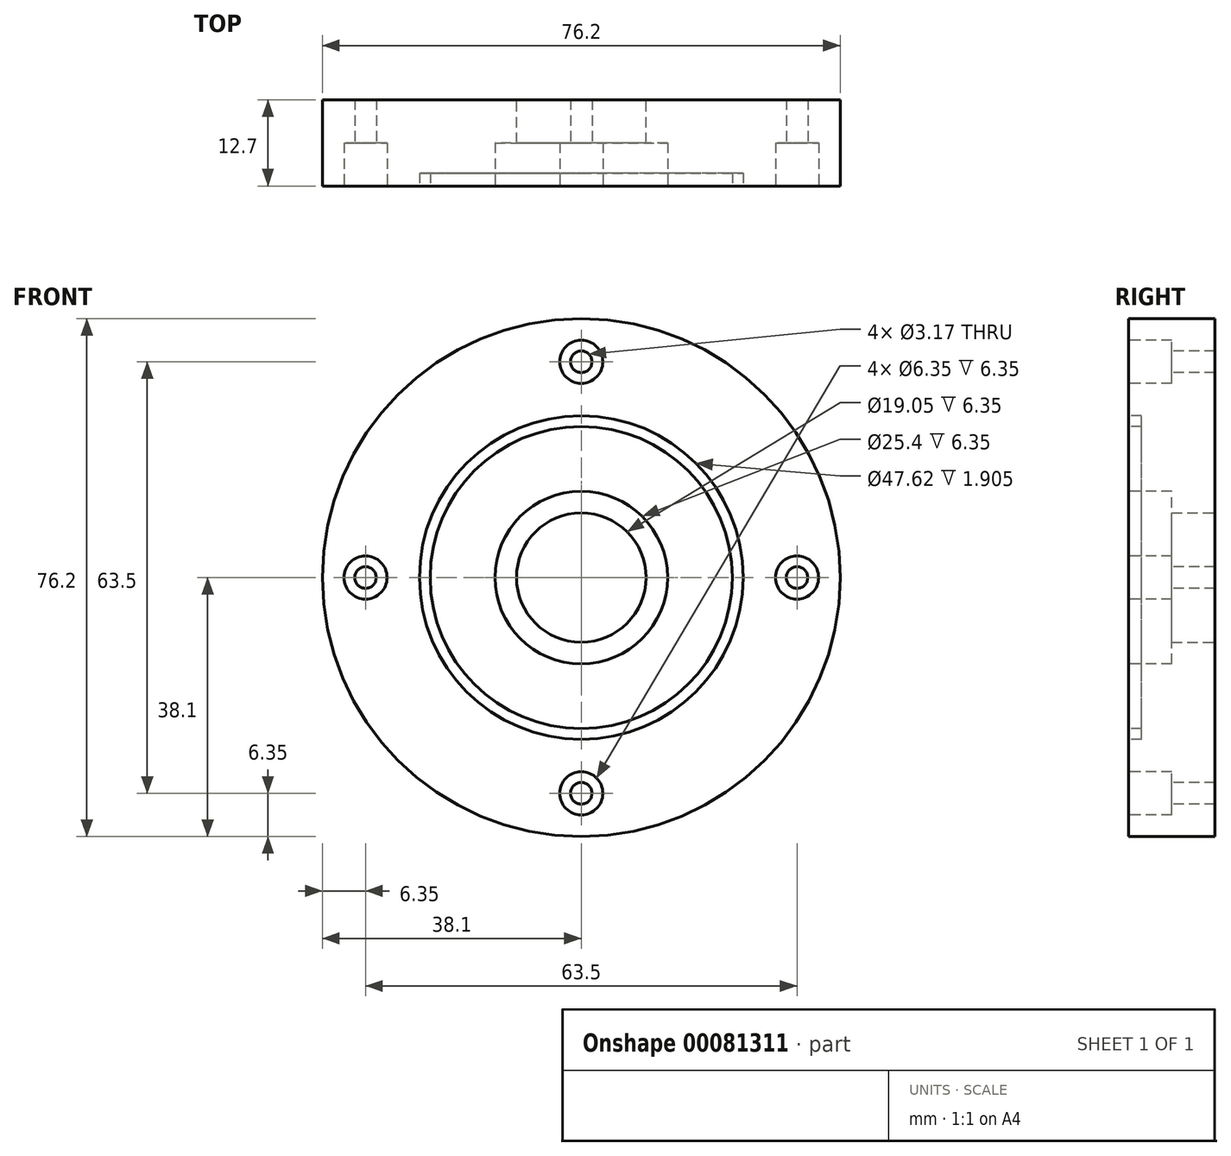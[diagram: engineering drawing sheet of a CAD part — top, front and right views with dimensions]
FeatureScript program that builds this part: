
annotation { "Feature Type Name" : "Feature", "Feature Type Description" : "" }
export const myFeature = defineFeature(function(context is Context, id is Id, definition is map)
    precondition{}
    {
        {
            var Q0;
            Q0=qCreatedBy(makeId("Front.planeOp"),FACE);
            var sketch = newSketch(context, id + "F0", { "sketchPlane" : qUnion([Q0])});
            skCircle(sketch, "E0", {"center": v(0, 0) * mm, "radius": 38.1 * mm});
            skCircle(sketch, "E1", {"center": v(0, 0) * mm, "radius": 9.53 * mm});
            skSolve(sketch);
        }
        {
            var Q0;
            Q0 = qSketchRegion(id + "F0", true);
            extrude(context, id + "F1", {"entities" : qUnion([Q0]), "depth" : 12.7 * mm});
        }
        {
            var Q0;
            Q0=makeQuery(id+"F1.opExtrude","CAP_FACE",FACE,{"disambiguationData":[OSD([sQuery(id+"F0.wireOp",EDGE,"E0"),sQuery(id+"F0.wireOp",EDGE,"E1")])],"isStart":false});
            var sketch = newSketch(context, id + "F2", { "sketchPlane" : qUnion([Q0])});
            skCircle(sketch, "E2", {"center": v(0, 0) * mm, "radius": 12.7 * mm});
            skSolve(sketch);
        }
        {
            var Q0;
            Q0=makeQuery(id+"F2.imprint","IMPRINT",FACE,{"disambiguationData":[TD([[makeQuery(id+"F2.imprint","IMPRINT",EDGE,{"derivedFrom":sQuery(id+"F2.wireOp",EDGE,"E2")}),1.0]])]});
            extrude(context, id + "F3", {"entities" : qUnion([Q0]), "operationType" : NewBodyOperationType.REMOVE, "oppositeDirection" : true, "depth" : 6.35 * mm});
        }
        {
            var Q0;
            Q0=makeQuery(id+"F1.opExtrude","CAP_FACE",FACE,{"disambiguationData":[OSD([sQuery(id+"F0.wireOp",EDGE,"E0"),sQuery(id+"F0.wireOp",EDGE,"E1")])],"isStart":false});
            var sketch = newSketch(context, id + "F4", { "sketchPlane" : qUnion([Q0])});
            skPoint(sketch, "E3", {"position": v(0, 31.75) * mm});
            skPoint(sketch, "E4", {"position": v(31.75, 0) * mm});
            skPoint(sketch, "E5", {"position": v(0, -31.75) * mm});
            skPoint(sketch, "E6", {"position": v(-31.75, 0) * mm});
            skSolve(sketch);
        }
        {
            var Q0;
            Q0=sQuery(id+"F4.wireOp",VERTEX,"E3");
            var Q1;
            Q1=sQuery(id+"F4.wireOp",VERTEX,"E6");
            var Q2;
            Q2=sQuery(id+"F4.wireOp",VERTEX,"E4");
            var Q3;
            Q3=sQuery(id+"F4.wireOp",VERTEX,"E5");
            var Q4;
            Q4=makeQuery(id+"F1.opExtrude","SWEPT_BODY",BODY,{"disambiguationData":[OSD([sQuery(id+"F0.wireOp",EDGE,"E0"),sQuery(id+"F0.wireOp",EDGE,"E1")])]});
            hole(context, id + "F5", {"style" : HoleStyle.C_BORE, "endStyle" : HoleEndStyle.THROUGH, "holeDiameter" : 3.17 * mm, "cBoreDiameter" : 6.35 * mm, "cBoreDepth" : 6.35 * mm, "locations" : qUnion([Q0, Q1, Q2, Q3]), "scope" : qUnion([Q4]), "isTappedThrough" : true});
        }
        {
            var Q0;
            Q0=makeQuery(id+"F1.opExtrude","CAP_FACE",FACE,{"disambiguationData":[OSD([sQuery(id+"F0.wireOp",EDGE,"E0"),sQuery(id+"F0.wireOp",EDGE,"E1")])],"isStart":false});
            var sketch = newSketch(context, id + "F6", { "sketchPlane" : qUnion([Q0])});
            skCircle(sketch, "E7", {"center": v(0, 0) * mm, "radius": 23.81 * mm});
            skCircle(sketch, "E8", {"center": v(0, 0) * mm, "radius": 22.23 * mm});
            skSolve(sketch);
        }
        {
            var Q0;
            Q0=makeQuery(id+"F6.imprint","IMPRINT",FACE,{"disambiguationData":[TD([[makeQuery(id+"F6.imprint","IMPRINT",EDGE,{"derivedFrom":sQuery(id+"F6.wireOp",EDGE,"E7")}),1.0]])]});
            extrude(context, id + "F7", {"entities" : qUnion([Q0]), "operationType" : NewBodyOperationType.REMOVE, "oppositeDirection" : true, "depth" : 1.9 * mm});
        }
    });
